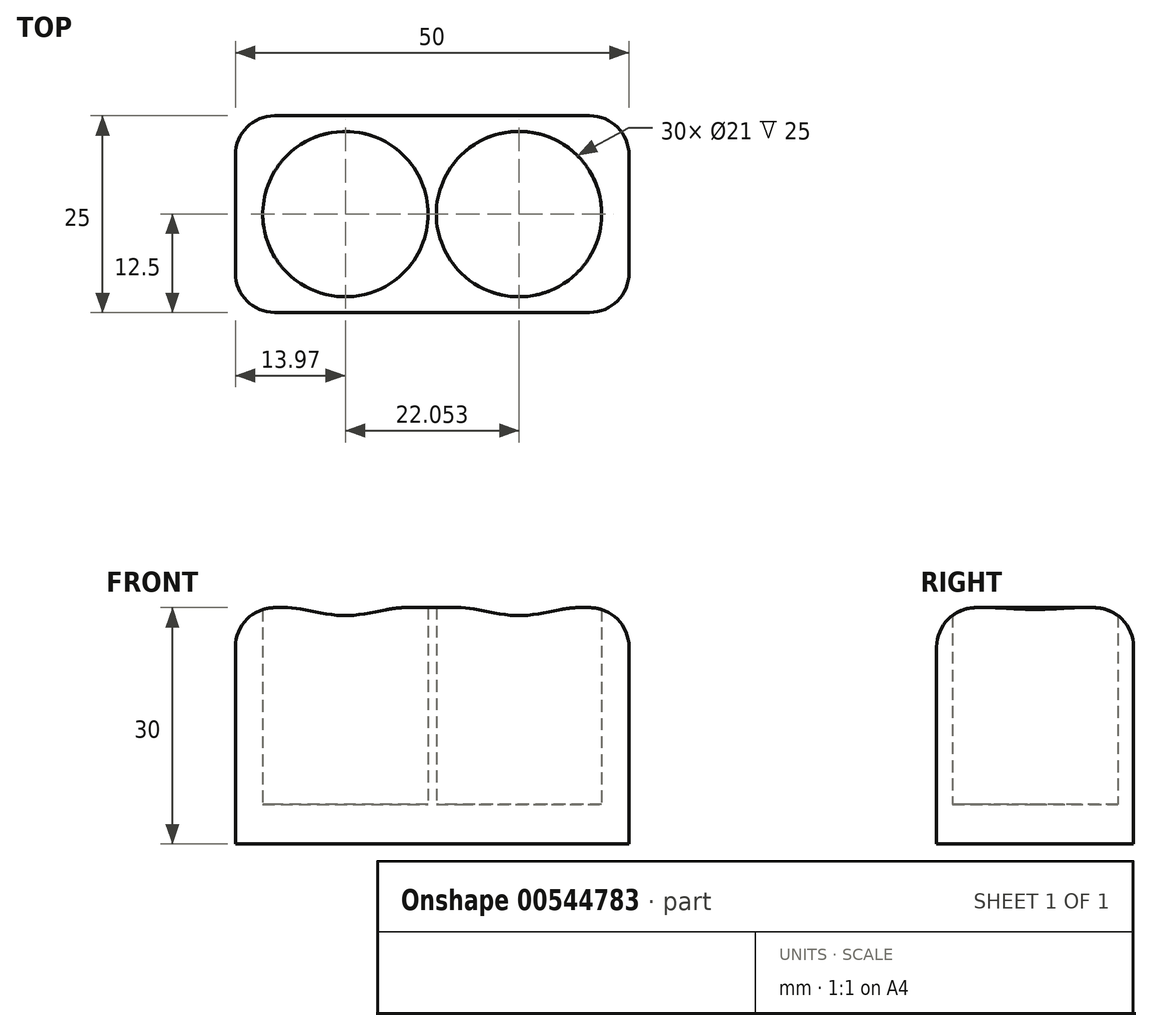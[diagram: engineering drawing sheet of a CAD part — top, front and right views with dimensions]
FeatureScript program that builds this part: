
annotation { "Feature Type Name" : "Feature", "Feature Type Description" : "" }
export const myFeature = defineFeature(function(context is Context, id is Id, definition is map)
    precondition{}
    {
        {
            var Q0;
            Q0=qCreatedBy(makeId("Top.planeOp"),FACE);
            var sketch = newSketch(context, id + "F0", { "sketchPlane" : qUnion([Q0])});
            skCircle(sketch, "E0", {"center": v(0, 0) * mm, "radius": 10.5 * mm});
            skCircle(sketch, "E1", {"center": v(22.05, 0) * mm, "radius": 10.5 * mm});
            skPoint(sketch, "E2", {"position": v(11.03, 0) * mm});
            skLineSegment(sketch, "E3", {"start": v(11.03, 0) * mm, "end": v(10.5, 0) * mm});
            skLineSegment(sketch, "E4", {"start": v(10.5, 0) * mm, "end": v(11.03, 0) * mm, "construction": true});
            skLineSegment(sketch, "E5", {"start": v(11.03, 0) * mm, "end": v(11.55, 0) * mm, "construction": true});
            skSolve(sketch);
        }
        {
            var Q0;
            Q0=qCreatedBy(makeId("Top.planeOp"),FACE);
            var sketch = newSketch(context, id + "F1", { "sketchPlane" : qUnion([Q0])});
            skLineSegment(sketch, "E6.bottom", {"start": v(-8.97, 12.5) * mm, "end": v(31.03, 12.5) * mm});
            skLineSegment(sketch, "E6.top", {"start": v(-8.97, -12.5) * mm, "end": v(31.03, -12.5) * mm});
            skLineSegment(sketch, "E6.left", {"start": v(-13.97, 7.5) * mm, "end": v(-13.97, -7.5) * mm});
            skLineSegment(sketch, "E6.right", {"start": v(36.03, 7.5) * mm, "end": v(36.03, -7.5) * mm});
            skPoint(sketch, "E7.visualSharp", {"position": v(-13.97, 12.5) * mm});
            skArc(sketch, "E7.filletArc", {"start": v(-8.97, 12.5) * mm, "mid": v(-12.5, 11.04) * mm, "end": v(-13.97, 7.5) * mm});
            skPoint(sketch, "E8.visualSharp", {"position": v(36.03, 12.5) * mm});
            skArc(sketch, "E8.filletArc", {"start": v(36.03, 7.5) * mm, "mid": v(34.56, 11.04) * mm, "end": v(31.03, 12.5) * mm});
            skPoint(sketch, "E9.visualSharp", {"position": v(36.03, -12.5) * mm});
            skArc(sketch, "E9.filletArc", {"start": v(31.03, -12.5) * mm, "mid": v(34.56, -11.04) * mm, "end": v(36.03, -7.5) * mm});
            skPoint(sketch, "E10.visualSharp", {"position": v(-13.97, -12.5) * mm});
            skArc(sketch, "E10.filletArc", {"start": v(-13.97, -7.5) * mm, "mid": v(-12.5, -11.04) * mm, "end": v(-8.97, -12.5) * mm});
            skSolve(sketch);
        }
        {
            var Q0;
            Q0=makeQuery(id+"F1.imprint","IMPRINT",FACE,{"disambiguationData":[TD([[makeQuery(id+"F1.imprint","IMPRINT",EDGE,{"derivedFrom":sQuery(id+"F1.wireOp",EDGE,"E6.bottom")}),-1.0]])]});
            extrude(context, id + "F2", {"entities" : qUnion([Q0]), "depth" : 30 * mm, "offsetDistance" : 25 * mm});
        }
        {
            var Q0;
            Q0=makeQuery(id+"F0.imprint","IMPRINT",FACE,{"disambiguationData":[TD([[makeQuery(id+"F0.imprint","IMPRINT",EDGE,{"derivedFrom":sQuery(id+"F0.wireOp",EDGE,"E0")}),1.0]])]});
            var Q1;
            Q1=makeQuery(id+"F0.imprint","IMPRINT",FACE,{"disambiguationData":[TD([[makeQuery(id+"F0.imprint","IMPRINT",EDGE,{"derivedFrom":sQuery(id+"F0.wireOp",EDGE,"E1")}),1.0]])]});
            extrude(context, id + "F3", {"entities" : qUnion([Q0, Q1]), "operationType" : NewBodyOperationType.REMOVE, "depth" : 60 * mm, "offsetDistance" : 25 * mm, "hasSecondDirection" : true, "secondDirectionOppositeDirection" : false, "secondDirectionDepth" : 5 * mm});
        }
        {
            var Q0;
            Q0=makeQuery(id+"F2.opExtrude","CAP_EDGE",EDGE,{"disambiguationData":[OSD([sQuery(id+"F1.wireOp",EDGE,"E6.top")])],"isStart":false});
            var Q1;
            Q1=makeQuery(id+"F2.opExtrude","CAP_EDGE",EDGE,{"disambiguationData":[OSD([sQuery(id+"F1.wireOp",EDGE,"E9.filletArc")])],"isStart":false});
            var Q2;
            Q2=makeQuery(id+"F2.opExtrude","CAP_EDGE",EDGE,{"disambiguationData":[OSD([sQuery(id+"F1.wireOp",EDGE,"E6.right")])],"isStart":false});
            var Q3;
            Q3=makeQuery(id+"F2.opExtrude","CAP_EDGE",EDGE,{"disambiguationData":[OSD([sQuery(id+"F1.wireOp",EDGE,"E8.filletArc")])],"isStart":false});
            var Q4;
            Q4=makeQuery(id+"F2.opExtrude","CAP_EDGE",EDGE,{"disambiguationData":[OSD([sQuery(id+"F1.wireOp",EDGE,"E6.bottom")])],"isStart":false});
            var Q5;
            Q5=makeQuery(id+"F2.opExtrude","CAP_EDGE",EDGE,{"disambiguationData":[OSD([sQuery(id+"F1.wireOp",EDGE,"E6.left")])],"isStart":false});
            var Q6;
            Q6=makeQuery(id+"F2.opExtrude","CAP_EDGE",EDGE,{"disambiguationData":[OSD([sQuery(id+"F1.wireOp",EDGE,"E7.filletArc")])],"isStart":false});
            var Q7;
            Q7=makeQuery(id+"F2.opExtrude","CAP_EDGE",EDGE,{"disambiguationData":[OSD([sQuery(id+"F1.wireOp",EDGE,"E10.filletArc")])],"isStart":false});
            fillet(context, id + "F4", {"entities" : qUnion([Q0, Q1, Q2, Q3, Q4, Q5, Q6, Q7]), "radius" : 5 * mm, "tangentPropagation" : true, "allowEdgeOverflow" : false});
        }
    });
